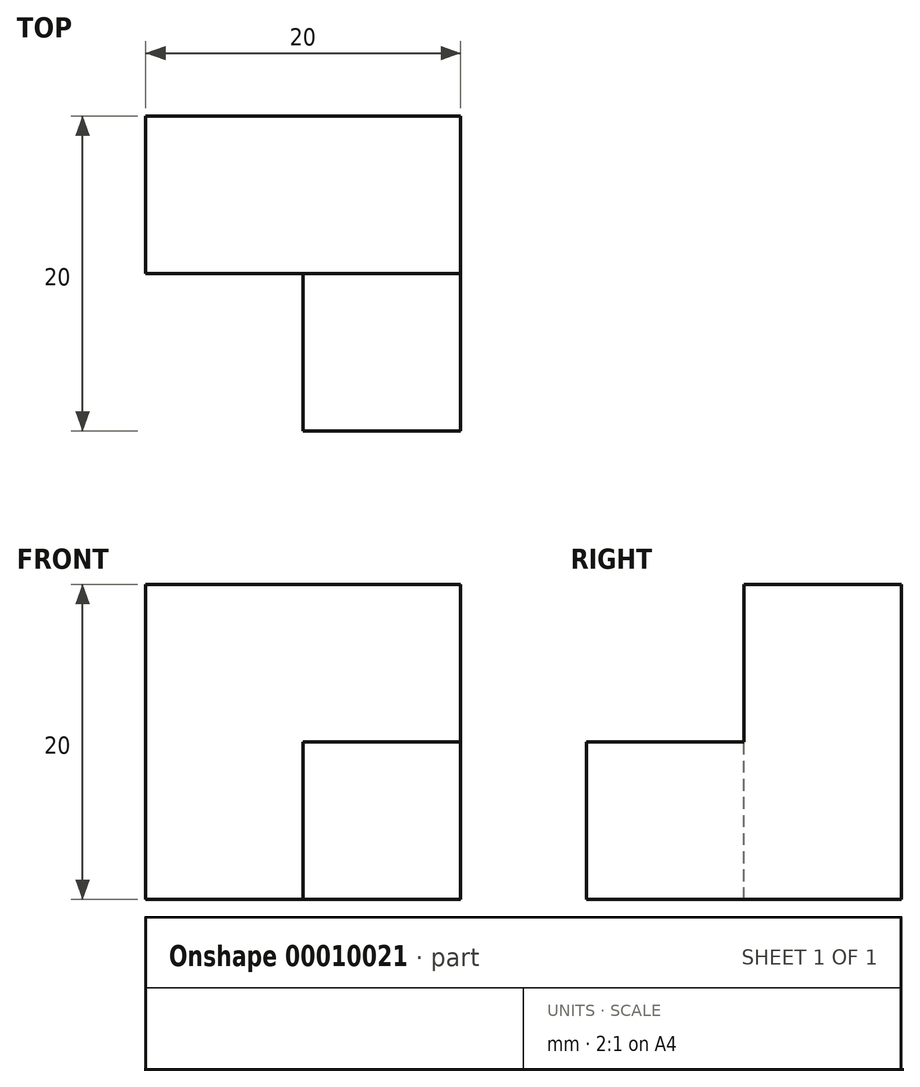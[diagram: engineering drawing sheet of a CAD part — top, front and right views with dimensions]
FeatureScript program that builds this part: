
annotation { "Feature Type Name" : "Feature", "Feature Type Description" : "" }
export const myFeature = defineFeature(function(context is Context, id is Id, definition is map)
    precondition{}
    {
        {
            var Q0;
            Q0=qCreatedBy(makeId("Front.planeOp"),FACE);
            var sketch = newSketch(context, id + "F0", { "sketchPlane" : qUnion([Q0])});
            skLineSegment(sketch, "E0.bottom", {"start": v(0, 0) * mm, "end": v(20, 0) * mm});
            skLineSegment(sketch, "E0.top", {"start": v(0, 20) * mm, "end": v(20, 20) * mm});
            skLineSegment(sketch, "E0.left", {"start": v(0, 0) * mm, "end": v(0, 20) * mm});
            skLineSegment(sketch, "E0.right", {"start": v(20, 0) * mm, "end": v(20, 20) * mm});
            skLineSegment(sketch, "E1.bottom", {"start": v(20, 0) * mm, "end": v(10, 0) * mm});
            skLineSegment(sketch, "E1.top", {"start": v(20, 10) * mm, "end": v(10, 10) * mm});
            skLineSegment(sketch, "E1.left", {"start": v(20, 0) * mm, "end": v(20, 10) * mm});
            skLineSegment(sketch, "E1.right", {"start": v(10, 0) * mm, "end": v(10, 10) * mm});
            skSolve(sketch);
        }
        {
            var Q0;
            Q0=makeQuery(id+"F0.imprint","IMPRINT",FACE,{"disambiguationData":[TD([[makeQuery(id+"F0.imprint","IMPRINT",EDGE,{"derivedFrom":sQuery(id+"F0.wireOp",EDGE,"E0.bottom")}),1.0]])]});
            extrude(context, id + "F1", {"entities" : qUnion([Q0]), "depth" : 20 * mm});
        }
        {
            var Q0;
            Q0 = qSketchRegion(id + "F0", true);
            extrude(context, id + "F2", {"entities" : qUnion([Q0]), "operationType" : NewBodyOperationType.ADD, "depth" : 10 * mm});
        }
    });
